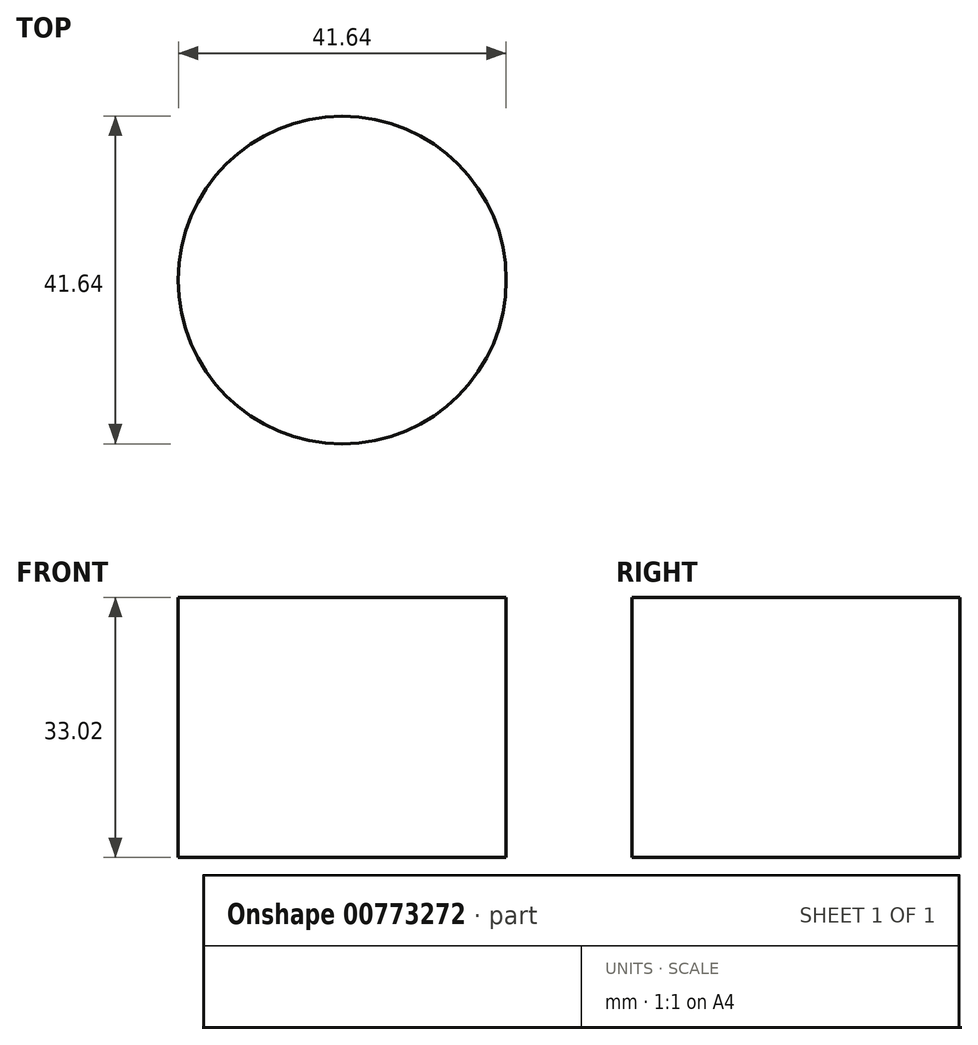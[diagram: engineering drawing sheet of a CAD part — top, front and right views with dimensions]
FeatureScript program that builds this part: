
annotation { "Feature Type Name" : "Feature", "Feature Type Description" : "" }
export const myFeature = defineFeature(function(context is Context, id is Id, definition is map)
    precondition{}
    {
        {
            var Q0;
            Q0=qCreatedBy(makeId("Top.planeOp"),FACE);
            var sketch = newSketch(context, id + "F0", { "sketchPlane" : qUnion([Q0])});
            skCircle(sketch, "E0", {"center": v(0, 0) * mm, "radius": 20.82 * mm});
            skSolve(sketch);
        }
        {
            var Q0;
            Q0 = qSketchRegion(id + "F0", true);
            extrude(context, id + "F1", {"entities" : qUnion([Q0]), "depth" : 33.02 * mm, "offsetDistance" : 25.4 * mm});
        }
    });
